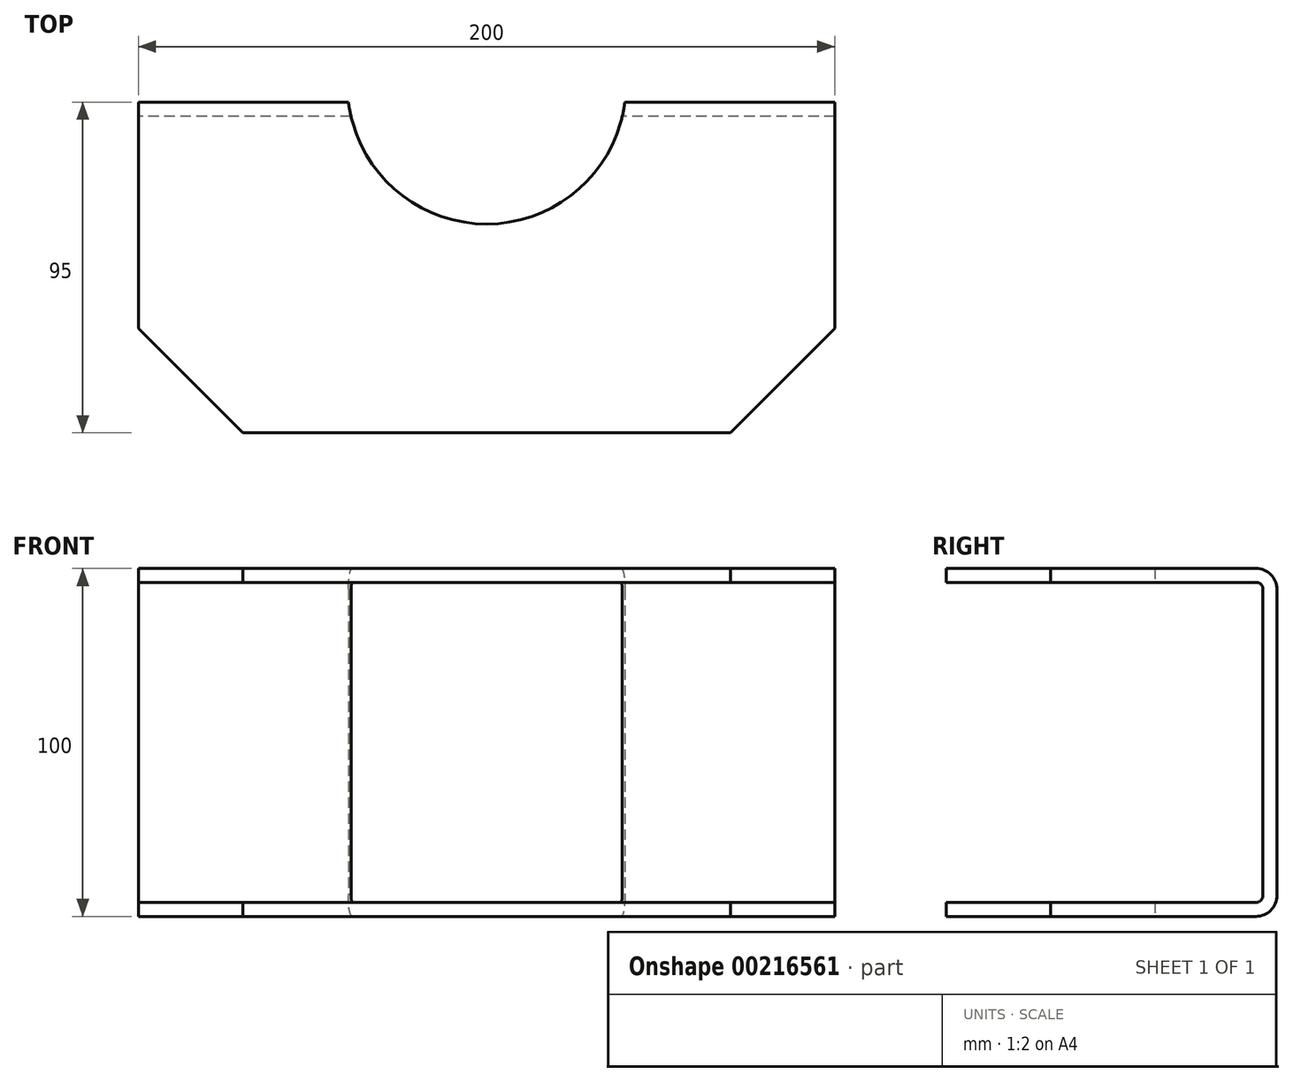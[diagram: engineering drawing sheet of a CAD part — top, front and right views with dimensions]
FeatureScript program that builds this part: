
annotation { "Feature Type Name" : "Feature", "Feature Type Description" : "" }
export const myFeature = defineFeature(function(context is Context, id is Id, definition is map)
    precondition{}
    {
        {
            var Q0;
            Q0=qCreatedBy(makeId("Right.planeOp"),FACE);
            var sketch = newSketch(context, id + "F0", { "sketchPlane" : qUnion([Q0])});
            skLineSegment(sketch, "E0", {"start": v(-5, 44) * mm, "end": v(-5, 0) * mm});
            skLineSegment(sketch, "E1", {"start": v(-11, 50) * mm, "end": v(-100, 50) * mm});
            skLineSegment(sketch, "E2", {"start": v(-70.48, 0) * mm, "end": v(67.12, 0) * mm, "construction": true});
            skLineSegment(sketch, "E3", {"start": v(-100, 46) * mm, "end": v(-11, 46) * mm});
            skLineSegment(sketch, "E4", {"start": v(-9, 44) * mm, "end": v(-9, 0) * mm});
            skArc(sketch, "E5.filletArc", {"start": v(-9, 44) * mm, "mid": v(-9.59, 45.41) * mm, "end": v(-11, 46) * mm});
            skPoint(sketch, "E6.visualSharp", {"position": v(-5, 50) * mm});
            skArc(sketch, "E6.filletArc", {"start": v(-5, 44) * mm, "mid": v(-6.76, 48.24) * mm, "end": v(-11, 50) * mm});
            skLineSegment(sketch, "E7", {"start": v(-100, 50) * mm, "end": v(-100, 46) * mm});
            skArc(sketch, "E8.MirrorCS", {"start": v(-5, -44) * mm, "mid": v(-6.76, -48.24) * mm, "end": v(-11, -50) * mm});
            skArc(sketch, "E9.MirrorCS", {"start": v(-9, -44) * mm, "mid": v(-9.59, -45.41) * mm, "end": v(-11, -46) * mm});
            skLineSegment(sketch, "E10.MirrorCS", {"start": v(-11, -50) * mm, "end": v(-100, -50) * mm});
            skLineSegment(sketch, "E11.MirrorCS", {"start": v(-100, -46) * mm, "end": v(-11, -46) * mm});
            skLineSegment(sketch, "E12.MirrorCS", {"start": v(-100, -50) * mm, "end": v(-100, -46) * mm});
            skLineSegment(sketch, "E13.MirrorCS", {"start": v(-9, -44) * mm, "end": v(-9, 0) * mm});
            skLineSegment(sketch, "E14.MirrorCS", {"start": v(-5, -44) * mm, "end": v(-5, 0) * mm});
            skSolve(sketch);
        }
        {
            var Q0;
            Q0 = qSketchRegion(id + "F0", true);
            extrude(context, id + "F1", {"entities" : qUnion([Q0]), "depth" : 100 * mm, "hasSecondDirection" : true, "secondDirectionOppositeDirection" : true, "secondDirectionDepth" : 100 * mm});
        }
        {
            var Q0;
            Q0=qCreatedBy(makeId("Top.planeOp"),FACE);
            var sketch = newSketch(context, id + "F2", { "sketchPlane" : qUnion([Q0])});
            skCircle(sketch, "E15", {"center": v(0, 0) * mm, "radius": 40 * mm});
            skSolve(sketch);
        }
        {
            var Q0;
            Q0 = qSketchRegion(id + "F2", true);
            extrude(context, id + "F3", {"entities" : qUnion([Q0]), "operationType" : NewBodyOperationType.REMOVE, "depth" : 100 * mm, "hasSecondDirection" : true, "secondDirectionOppositeDirection" : true, "secondDirectionDepth" : 100 * mm});
        }
        {
            var Q0;
            Q0=makeQuery(id+"F1.opExtrude","CAP_EDGE",EDGE,{"disambiguationData":[OSD([sQuery(id+"F0.wireOp",EDGE,"E12.MirrorCS")])],"isStart":false});
            var Q1;
            Q1=makeQuery(id+"F1.opExtrude","CAP_EDGE",EDGE,{"disambiguationData":[OSD([sQuery(id+"F0.wireOp",EDGE,"E7")])],"isStart":false});
            var Q2;
            Q2=makeQuery(id+"F1.opExtrude","CAP_EDGE",EDGE,{"disambiguationData":[OSD([sQuery(id+"F0.wireOp",EDGE,"E12.MirrorCS")])],"isStart":true});
            var Q3;
            Q3=makeQuery(id+"F1.opExtrude","CAP_EDGE",EDGE,{"disambiguationData":[OSD([sQuery(id+"F0.wireOp",EDGE,"E7")])],"isStart":true});
            chamfer(context, id + "F4", {"entities" : qUnion([Q0, Q1, Q2, Q3]), "width" : 30 * mm, "tangentPropagation" : true});
        }
    });
